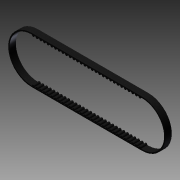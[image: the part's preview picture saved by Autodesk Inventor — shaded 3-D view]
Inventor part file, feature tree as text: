
AUTODESK INVENTOR PART (.ipt)
format: ipt  version: 2012 (Build 160160000, 160)  size: 402,944 bytes
history: native  units: in
note: dims shown in document units (in); Inventor stores cm internally (conversion verified against a paired STEP export)
features: extrude x1, sketch x1
ambient origin geometry x8: Origin, YZ Plane, XZ Plane, XY Plane, X Axis, Y Axis, Z Axis, Center Point
bodies: Solid1 (feature_tree)
feature tree (2):
  extrude  "Extrusion1"  Depth=1.231in
  sketch  "Sketch1"  dims[d0=6.125in d1=1.231in d2=1.3in d4=0.0625in d5=0.024in d6=0.01in d7=11.811in d9=0.204in d10=0.3937in d12=1.0in d14=0.3543in d15=0.0in d16=1.231in]
